# Revit family: 303_R31X_
name_source: partatom
category: Pipe Accessories
revit_build: Autodesk Revit 2018 (Build: 20170223_1515(x64)
units: mm (PartAtom-declared; Revit-internal decimal feet)

## family parameters
Always vertical = Yes
Cut with Voids When Loaded = No
Part Type = Valve - Breaks Into
Round Connector Dimension = Use Diameter
Shared = No
Work Plane-Based = No

## types (5) — shared parameters
CAT0 = Yes
CenSd_W2_6 = 13 mm
Description = Straight lockshield valve for heat systems
J6 = 18 mm  [stored 0.0590551 ft]
L2D_Min = 3048 mm
L5 = 4 mm  [stored 0.0131234 ft]
L8 = 2 mm  [stored 0.00656168 ft]
L8__ve = -2 mm  [stored -0.00656168 ft]
M1 = 18 mm  [stored 0.0590551 ft]
M11 = 21 mm  [stored 0.0688976 ft]
Manufacturer = Giacomini
QmdConnectorList = 301;D;302;D1
URL = http://www.giacomini.com
W2 = 15 mm  [stored 0.0492126 ft]
W4 = 12 mm  [stored 0.0393701 ft]
magiPartTypeId = 303
magiProductFamilyId = R31X*
zero-valued in all types: MC_Default_elevation

## per-type parameters (varying)
| type | B3 | B4 | D | D1 | G3 | J5 | K3 | L2 | L2D | L6 | L6__ve | LC | LC1 | LC2 | LX | M12 | R1 | SW1 | SW2 | W2D | X11 |
| R31X032 | 6 mm  [stored 0.019685 ft] | 4 mm  [stored 0.0131234 ft] | 16 mm | 10 mm | 10 mm  [stored 0.0328084 ft] | 3 mm  [stored 0.00984252 ft] | 7 mm  [stored 0.0229659 ft] | 9 mm  [stored 0.0295276 ft] | 56 mm | 4 mm  [stored 0.0131234 ft] | -4 mm  [stored -0.0131234 ft] | 52 mm  [stored 0.170604 ft] | 28 mm  [stored 0.0918635 ft] | 37 mm | 34 mm | 7 mm  [stored 0.0229659 ft] | 8 mm  [stored 0.0262467 ft] | Yes | No | 16 mm  [stored 0.0524934 ft] | 13 mm |
| R31X036 | 9 mm  [stored 0.0295276 ft] | 6 mm  [stored 0.019685 ft] | 22 mm | 20 mm | 15 mm  [stored 0.0492126 ft] | 14 mm  [stored 0.0459318 ft] | 10 mm  [stored 0.0328084 ft] | 10 mm  [stored 0.0328084 ft] | 63 mm | 5 mm  [stored 0.0164042 ft] | -5 mm  [stored -0.0164042 ft] | 54 mm | 32 mm | 42 mm  [stored 0.137795 ft] | 39 mm | 11 mm | 13 mm | No | Yes | 22 mm | 15 mm  [stored 0.0492126 ft] |
| R31X035 | 7 mm  [stored 0.0229659 ft] | 5 mm  [stored 0.0164042 ft] | 18 mm | 20 mm | 15 mm  [stored 0.0492126 ft] | 14 mm  [stored 0.0459318 ft] | 8 mm  [stored 0.0262467 ft] | 9 mm  [stored 0.0295276 ft] | 60 mm | 5 mm  [stored 0.0164042 ft] | -5 mm  [stored -0.0164042 ft] | 54 mm | 30 mm  [stored 0.0984252 ft] | 40 mm | 37 mm | 11 mm | 13 mm | No | Yes | 18 mm  [stored 0.0590551 ft] | 14 mm  [stored 0.0459318 ft] |
| R31X034 | 7 mm  [stored 0.0229659 ft] | 5 mm  [stored 0.0164042 ft] | 18 mm | 15 mm | 12 mm  [stored 0.0393701 ft] | 3 mm  [stored 0.00984252 ft] | 8 mm  [stored 0.0262467 ft] | 9 mm  [stored 0.0295276 ft] | 58 mm | 4 mm  [stored 0.0131234 ft] | -4 mm  [stored -0.0131234 ft] | 52 mm  [stored 0.170604 ft] | 29 mm | 39 mm | 35 mm  [stored 0.114829 ft] | 11 mm | 11 mm | No | Yes | 18 mm  [stored 0.0590551 ft] | 13 mm |
| R31X033 | 6 mm  [stored 0.019685 ft] | 4 mm  [stored 0.0131234 ft] | 16 mm | 15 mm | 12 mm  [stored 0.0393701 ft] | 3 mm  [stored 0.00984252 ft] | 7 mm  [stored 0.0229659 ft] | 9 mm  [stored 0.0295276 ft] | 57 mm | 4 mm  [stored 0.0131234 ft] | -4 mm  [stored -0.0131234 ft] | 52 mm  [stored 0.170604 ft] | 29 mm | 38 mm | 35 mm  [stored 0.114829 ft] | 7 mm  [stored 0.0229659 ft] | 11 mm | Yes | No | 16 mm  [stored 0.0524934 ft] | 13 mm |

note: column(s) folded — value = type name in every type: magiProductCode, magiProductId

note: [stored X ft] marks values corroborated as IEEE doubles in the binary element streams (Revit-internal decimal feet)

## geometry (parser evidence)
native form markers: Sweep x2
no freeform markers — native parametric forms only
